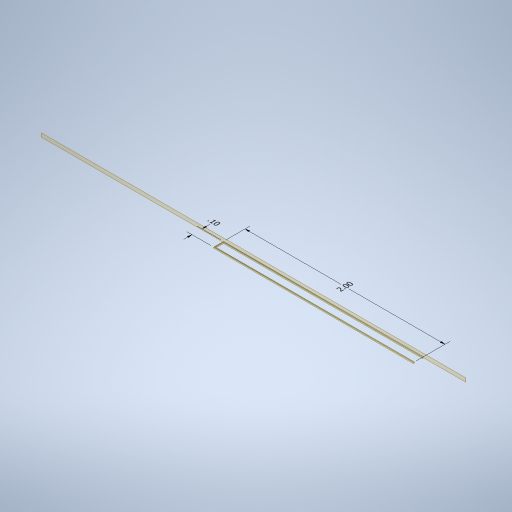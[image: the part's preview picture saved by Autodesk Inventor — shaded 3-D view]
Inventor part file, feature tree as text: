
AUTODESK INVENTOR PART (.ipt)
format: ipt  version: 2024.2 (Build 282272000, 272)  size: 275,968 bytes
history: native  units: in
note: dims shown in document units (in); Inventor stores cm internally (conversion verified against a paired STEP export)
features: other x3, plane x3, sketch x2, sweep x1
ambient origin geometry x8: Origin, YZ Plane, XZ Plane, XY Plane, X Axis, Y Axis, Z Axis, Center Point
bodies: Solid1 (feature_tree)
feature tree (9):
  other  "Annotations"
  sweep  "Sweep1"
  plane  "Work Plane1"
  plane  "Work Plane2"
  plane  "Work Plane4"
  sketch  "Sketch1"  dims[d6=0.0in d7=0.0in d11=0.25in d19=-0.25in]
  sketch  "Sketch2"  dims[d69=2.0in d70=2.0in d86=-0.1175in d89=0.1in d90=0.0in d91=0.0in d92=0.0in d98=0.01in d99=0.01in d100=0.1997in d101=2.0in d102=0.2692in d103=0.1197in d104=0.1in]
  other  "Linear Dimension 1"
  other  "Linear Dimension 2"
